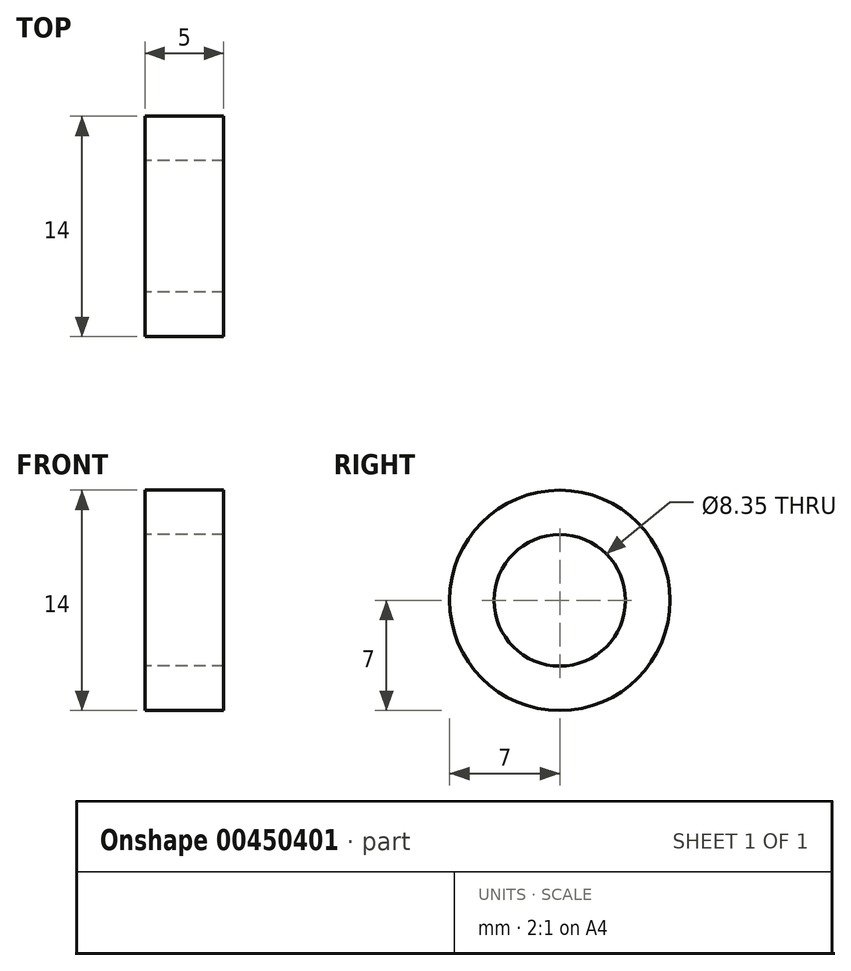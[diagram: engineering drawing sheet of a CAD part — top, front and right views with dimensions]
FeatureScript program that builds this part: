
annotation { "Feature Type Name" : "Feature", "Feature Type Description" : "" }
export const myFeature = defineFeature(function(context is Context, id is Id, definition is map)
    precondition{}
    {
        {
            var Q0;
            Q0=qCreatedBy(makeId("Front.planeOp"),FACE);
            var sketch = newSketch(context, id + "F0", { "sketchPlane" : qUnion([Q0])});
            skLineSegment(sketch, "E0.bottom", {"start": v(0.3, 7) * mm, "end": v(5.3, 7) * mm});
            skLineSegment(sketch, "E0.top", {"start": v(0.3, 4.17) * mm, "end": v(5.3, 4.17) * mm});
            skLineSegment(sketch, "E0.left", {"start": v(0.3, 7) * mm, "end": v(0.3, 4.17) * mm});
            skLineSegment(sketch, "E0.right", {"start": v(5.3, 7) * mm, "end": v(5.3, 4.17) * mm});
            skLineSegment(sketch, "E1.MirrorCS", {"start": v(0.3, -7) * mm, "end": v(5.3, -7) * mm});
            skLineSegment(sketch, "E2.MirrorCS", {"start": v(5.3, -7) * mm, "end": v(5.3, -4.17) * mm});
            skLineSegment(sketch, "E3.MirrorCS", {"start": v(0.3, -7) * mm, "end": v(0.3, -4.17) * mm});
            skLineSegment(sketch, "E4.MirrorCS", {"start": v(0.3, -4.17) * mm, "end": v(5.3, -4.17) * mm});
            skLineSegment(sketch, "E5", {"start": v(-3.63, 0) * mm, "end": v(12.58, 0) * mm, "construction": true});
            skSolve(sketch);
        }
        {
            var Q0;
            Q0=makeQuery(id+"F0.imprint","IMPRINT",FACE,{"disambiguationData":[TD([[makeQuery(id+"F0.imprint","IMPRINT",EDGE,{"derivedFrom":sQuery(id+"F0.wireOp",EDGE,"E0.bottom")}),-1.0]])]});
            var Q1;
            Q1=sQuery(id+"F0.wireOp",EDGE,"E5");
            revolve(context, id + "F1", {"entities" : qUnion([Q0]), "axis" : qUnion([Q1]), "revolveType" : RevolveType.FULL});
        }
    });
